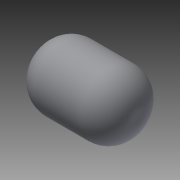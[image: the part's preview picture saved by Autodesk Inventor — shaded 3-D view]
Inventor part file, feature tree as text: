
AUTODESK INVENTOR PART (.ipt)
format: ipt  version: 2015 SP1 (Build 190203100, 203)  size: 125,952 bytes
history: native  units: in
note: dims shown in document units (in); Inventor stores cm internally (conversion verified against a paired STEP export)
features: revolve x1, sketch x1
ambient origin geometry x8: Origin, YZ Plane, XZ Plane, XY Plane, X Axis, Y Axis, Z Axis, Center Point
bodies: Solid1 (feature_tree)
feature tree (2):
  revolve  "Revolution1"  [1 undecoded]
  sketch  "Sketch1"  dims[d0=3.05in d1=0.5in d2=9.1in d3=90.0deg]
note: 1 required parameter value undecoded (feature->parameter linkage not recoverable at this tier; creation-order binding heuristic only, values carry confidence <= 0.55)
